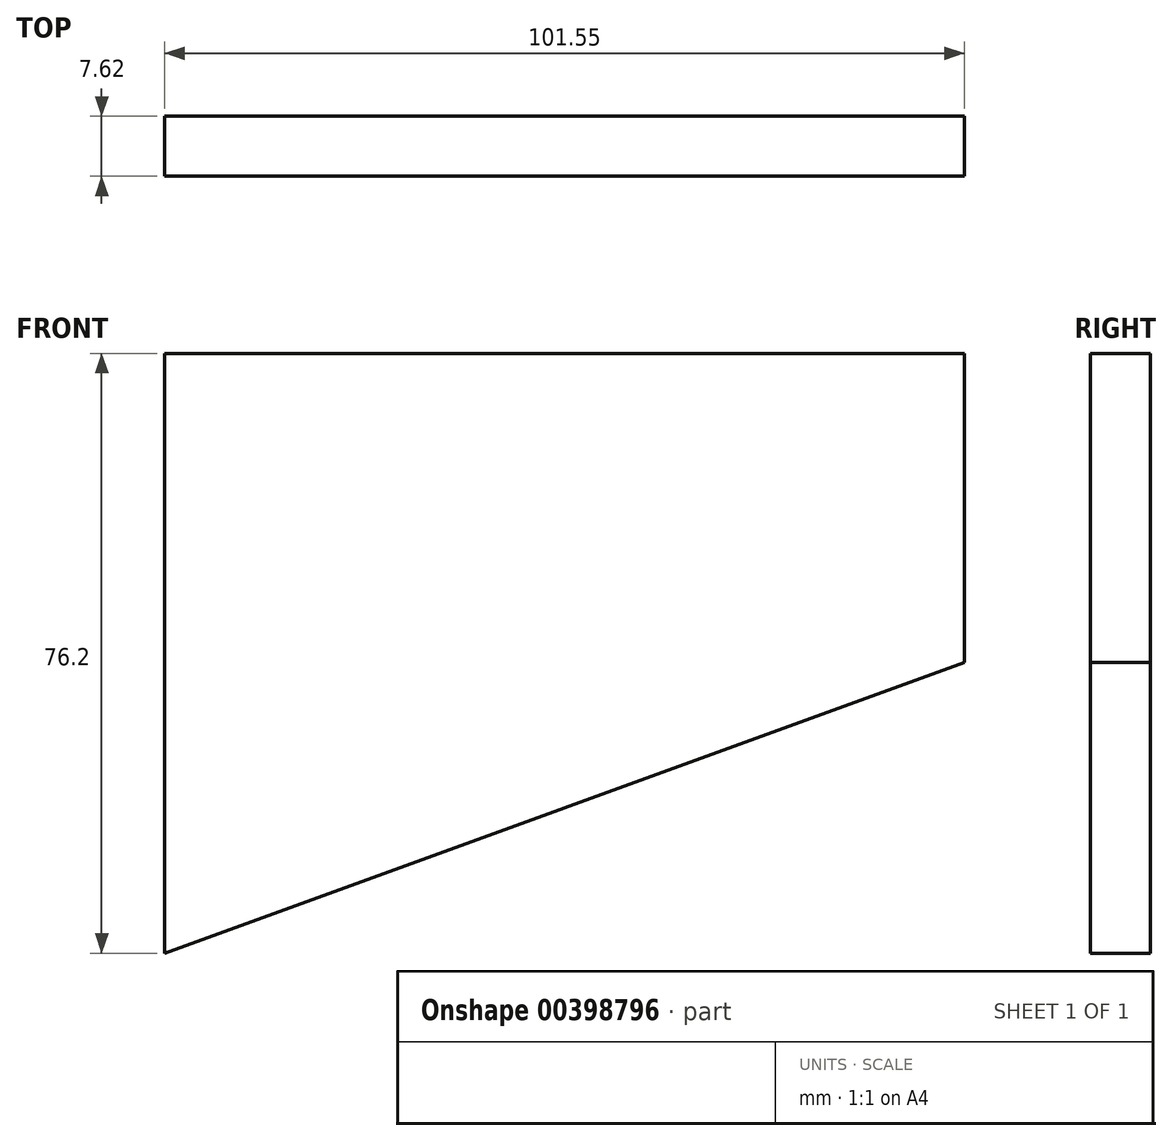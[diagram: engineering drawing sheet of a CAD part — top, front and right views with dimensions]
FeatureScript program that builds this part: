
annotation { "Feature Type Name" : "Feature", "Feature Type Description" : "" }
export const myFeature = defineFeature(function(context is Context, id is Id, definition is map)
    precondition{}
    {
        {
            var Q0;
            Q0=qCreatedBy(makeId("Front.planeOp"),FACE);
            var sketch = newSketch(context, id + "F0", { "sketchPlane" : qUnion([Q0])});
            skLineSegment(sketch, "E0.top", {"start": v(-36.03, 40.44) * mm, "end": v(0, 40.44) * mm});
            skLineSegment(sketch, "E0.left", {"start": v(-36.03, -35.76) * mm, "end": v(-36.03, 40.44) * mm});
            skLineSegment(sketch, "E1", {"start": v(0, 40.44) * mm, "end": v(65.52, 40.44) * mm});
            skLineSegment(sketch, "E2", {"start": v(-36.03, -35.76) * mm, "end": v(65.52, 1.2) * mm});
            skLineSegment(sketch, "E3", {"start": v(65.52, 40.44) * mm, "end": v(65.52, 1.2) * mm});
            skSolve(sketch);
        }
        {
            var Q0;
            Q0=makeQuery(id+"F0.imprint","IMPRINT",FACE,{"disambiguationData":[TD([[makeQuery(id+"F0.imprint","IMPRINT",EDGE,{"derivedFrom":sQuery(id+"F0.wireOp",EDGE,"E0.top")}),-1.0]])]});
            extrude(context, id + "F1", {"entities" : qUnion([Q0]), "depth" : 3.8 * mm, "hasSecondDirection" : true, "secondDirectionOppositeDirection" : true, "secondDirectionDepth" : 3.8 * mm});
        }
    });
